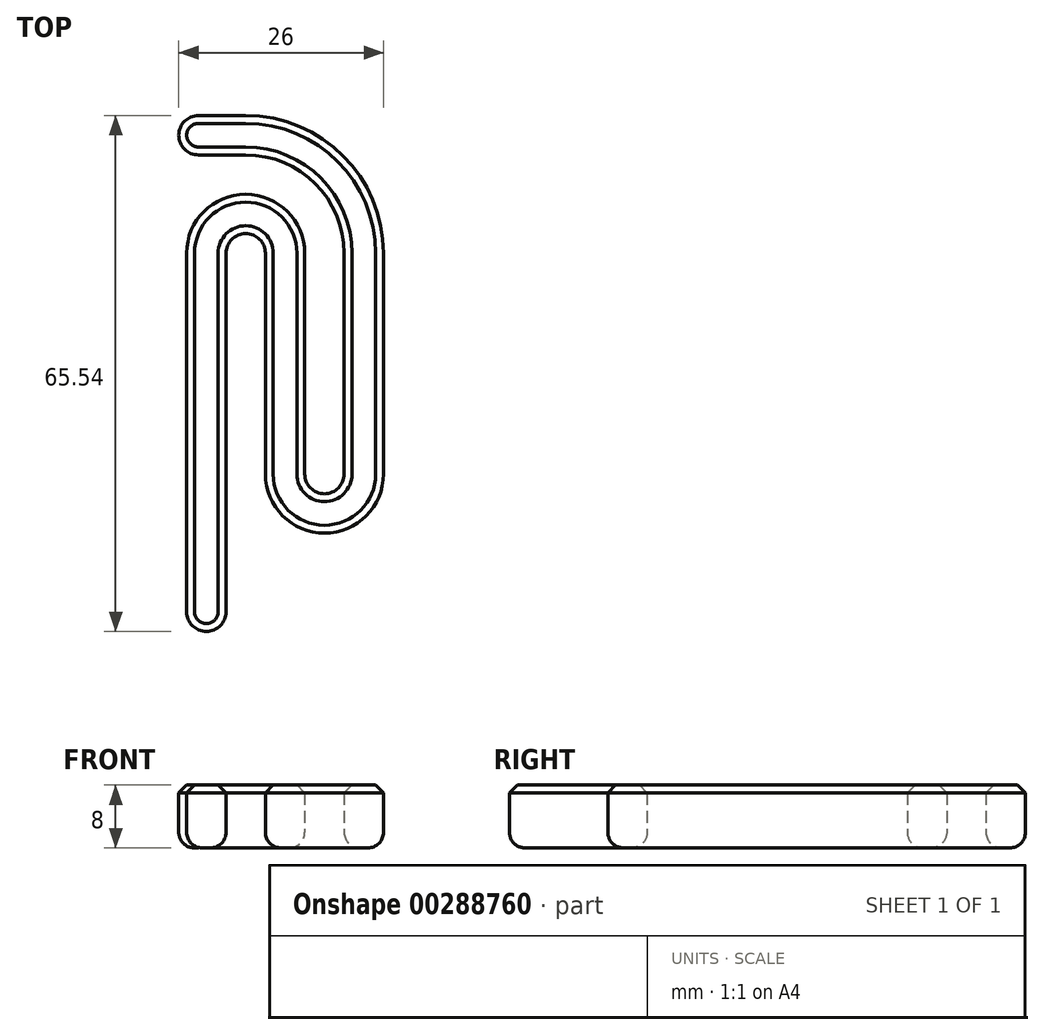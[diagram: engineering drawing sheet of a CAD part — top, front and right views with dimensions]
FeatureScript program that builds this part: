
annotation { "Feature Type Name" : "Feature", "Feature Type Description" : "" }
export const myFeature = defineFeature(function(context is Context, id is Id, definition is map)
    precondition{}
    {
        {
            var Q0;
            Q0=qCreatedBy(makeId("Top.planeOp"),FACE);
            var sketch = newSketch(context, id + "F0", { "sketchPlane" : qUnion([Q0])});
            skArc(sketch, "E0", {"start": v(-15.18, -13.58) * mm, "mid": v(-12.68, -16.08) * mm, "end": v(-10.18, -13.58) * mm});
            skArc(sketch, "E1", {"start": v(-20.18, 14.46) * mm, "mid": v(-22.68, 16.96) * mm, "end": v(-25.18, 14.46) * mm});
            skLineSegment(sketch, "E2", {"start": v(-25.18, 14.46) * mm, "end": v(-25.18, -16.08) * mm});
            skLineSegment(sketch, "E3", {"start": v(-10.18, -13.58) * mm, "end": v(-10.18, 14.46) * mm});
            skLineSegment(sketch, "E4", {"start": v(-3.3, -16.08) * mm, "end": v(-27.09, -16.08) * mm, "construction": true});
            skLineSegment(sketch, "E5", {"start": v(-1.5, 16.96) * mm, "end": v(-33.55, 16.96) * mm, "construction": true});
            skLineSegment(sketch, "E6", {"start": v(-20.18, 14.46) * mm, "end": v(-20.18, -13.58) * mm});
            skLineSegment(sketch, "E7", {"start": v(-15.18, -13.58) * mm, "end": v(-15.18, 14.46) * mm});
            skArc(sketch, "E8", {"start": v(-15.18, 14.46) * mm, "mid": v(-22.68, 21.96) * mm, "end": v(-30.18, 14.46) * mm});
            skArc(sketch, "E9", {"start": v(-15.18, -6.51) * mm, "mid": v(-12.68, -21.08) * mm, "end": v(-10.18, -6.51) * mm});
            skLineSegment(sketch, "E10", {"start": v(-5.18, -13.58) * mm, "end": v(-5.18, 14.46) * mm});
            skLineSegment(sketch, "E11", {"start": v(-30.18, 14.46) * mm, "end": v(-30.18, -16.08) * mm});
            skArc(sketch, "E12", {"start": v(-10.18, 14.46) * mm, "mid": v(-13.84, 23.3) * mm, "end": v(-22.68, 26.96) * mm});
            skArc(sketch, "E13", {"start": v(-5.18, 14.46) * mm, "mid": v(-10.3, 26.84) * mm, "end": v(-22.68, 31.96) * mm});
            skLineSegment(sketch, "E14", {"start": v(-22.68, 26.96) * mm, "end": v(-28.68, 26.96) * mm});
            skLineSegment(sketch, "E15", {"start": v(-28.68, 31.96) * mm, "end": v(-22.68, 31.96) * mm});
            skArc(sketch, "E16", {"start": v(-28.68, 31.96) * mm, "mid": v(-31.18, 29.46) * mm, "end": v(-28.68, 26.96) * mm});
            skLineSegment(sketch, "E17", {"start": v(-30.18, -16.08) * mm, "end": v(-30.18, -31.08) * mm});
            skLineSegment(sketch, "E18", {"start": v(-25.18, -31.08) * mm, "end": v(-25.18, -16.08) * mm});
            skArc(sketch, "E19", {"start": v(-30.18, -31.08) * mm, "mid": v(-27.68, -33.58) * mm, "end": v(-25.18, -31.08) * mm});
            skSolve(sketch);
        }
        {
            var Q0;
            {var subQ5=sQuery(id+"F0.wireOp",EDGE,"E1");Q0=makeQuery(id+"F0.imprint","IMPRINT",FACE,{"disambiguationData":[TD([[makeQuery(id+"F0.imprint","IMPRINT",EDGE,{"derivedFrom":subQ5}),-1.0]])]});}
            var Q1;
            {var subQ4=sQuery(id+"F0.wireOp",EDGE,"E11");Q1=makeQuery(id+"F0.imprint","IMPRINT",FACE,{"disambiguationData":[TD([[makeQuery(id+"F0.imprint","IMPRINT",EDGE,{"derivedFrom":subQ4}),1.0]])]});}
            var Q2;
            {var subQ0=sQuery(id+"F0.wireOp",EDGE,"E9");var subQ1=sQuery(id+"F0.wireOp",EDGE,"E6");var subQ2=makeQuery(id+"F0.imprint","INTERSECT",VERTEX,{"derivedFrom":[subQ1,subQ0]});Q2=makeQuery(id+"F0.imprint","IMPRINT",FACE,{"disambiguationData":[TD([[makeQuery(id+"F0.imprint","IMPRINT",EDGE,{"disambiguationData":[TD([[subQ2,1.0]])],"derivedFrom":subQ1}),1.0]])]});}
            var Q3;
            {var subQ4=sQuery(id+"F0.wireOp",EDGE,"E10");Q3=makeQuery(id+"F0.imprint","IMPRINT",FACE,{"disambiguationData":[TD([[makeQuery(id+"F0.imprint","IMPRINT",EDGE,{"derivedFrom":subQ4}),1.0]])]});}
            var Q4;
            {var subQ4=sQuery(id+"F0.wireOp",EDGE,"E0");Q4=makeQuery(id+"F0.imprint","IMPRINT",FACE,{"disambiguationData":[TD([[makeQuery(id+"F0.imprint","IMPRINT",EDGE,{"derivedFrom":subQ4}),-1.0]])]});}
            extrude(context, id + "F1", {"entities" : qUnion([Q0, Q1, Q2, Q3, Q4]), "depth" : 8 * mm});
        }
        {
            var Q0;
            Q0=makeQuery(id+"F1.opExtrude","CAP_EDGE",EDGE,{"disambiguationData":[OSD([sQuery(id+"F0.wireOp",EDGE,"E10")])],"isStart":true});
            fillet(context, id + "F2", {"entities" : qUnion([Q0]), "radius" : 2 * mm, "tangentPropagation" : true, "allowEdgeOverflow" : false});
        }
        {
            var Q0;
            Q0=makeQuery(id+"F1.opExtrude","CAP_EDGE",EDGE,{"disambiguationData":[OSD([sQuery(id+"F0.wireOp",EDGE,"E6")])],"isStart":false});
            chamfer(context, id + "F3", {"entities" : qUnion([Q0]), "width" : 1 * mm, "tangentPropagation" : true});
        }
    });
